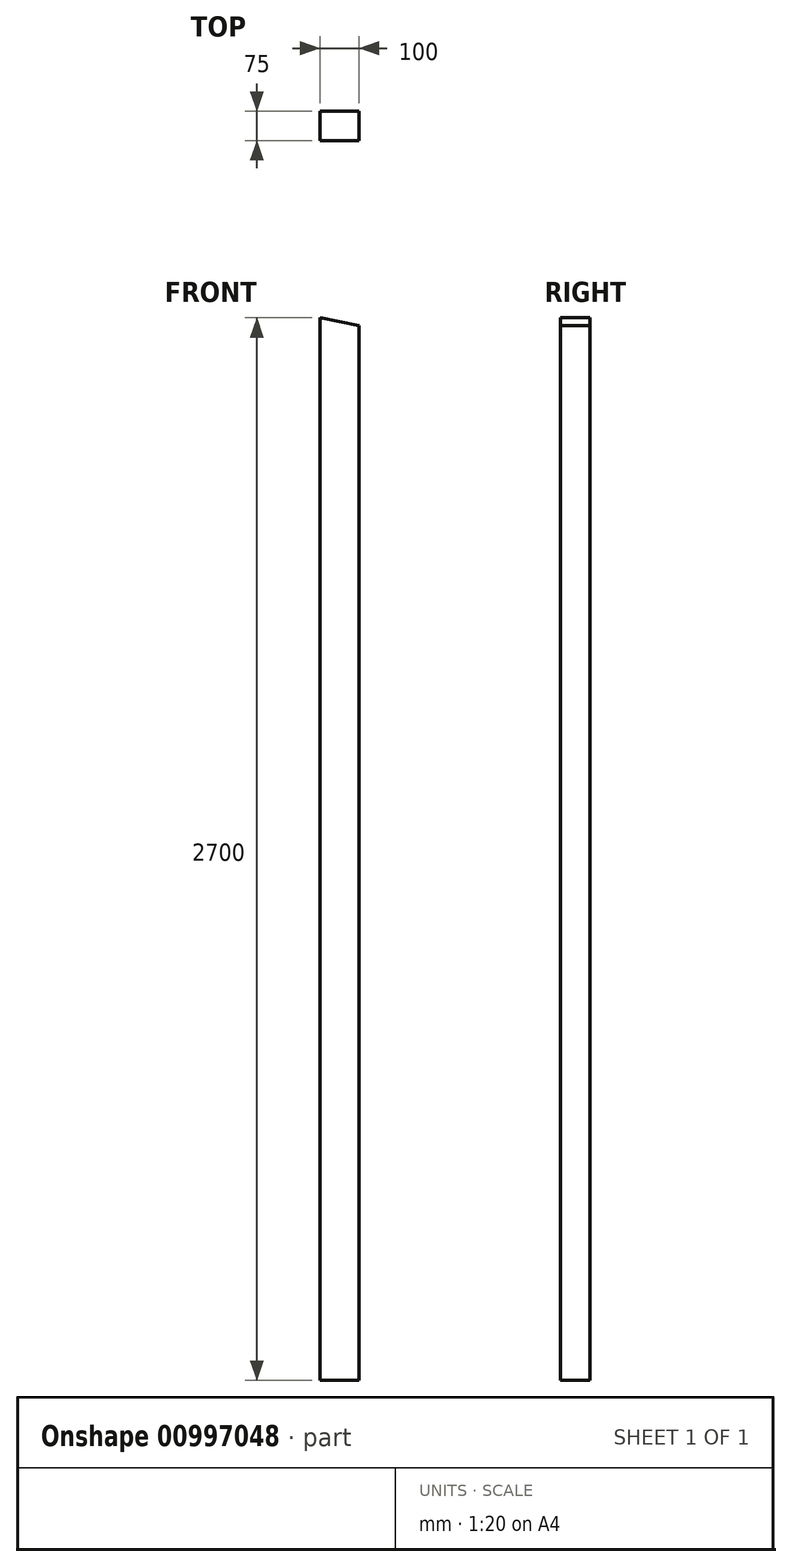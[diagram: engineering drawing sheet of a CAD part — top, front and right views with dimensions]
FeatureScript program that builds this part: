
annotation { "Feature Type Name" : "Feature", "Feature Type Description" : "" }
export const myFeature = defineFeature(function(context is Context, id is Id, definition is map)
    precondition{}
    {
        {
            var Q0;
            Q0=qCreatedBy(makeId("Top.planeOp"),FACE);
            var sketch = newSketch(context, id + "F0", { "sketchPlane" : qUnion([Q0])});
            skLineSegment(sketch, "E0.bottom", {"start": v(-89.27, 75) * mm, "end": v(10.73, 75) * mm});
            skLineSegment(sketch, "E0.top", {"start": v(-89.27, 0) * mm, "end": v(10.73, 0) * mm});
            skLineSegment(sketch, "E0.left", {"start": v(-89.27, 75) * mm, "end": v(-89.27, 0) * mm});
            skLineSegment(sketch, "E0.right", {"start": v(10.73, 75) * mm, "end": v(10.73, 0) * mm});
            skSolve(sketch);
        }
        {
            var Q0;
            Q0 = qSketchRegion(id + "F0", true);
            extrude(context, id + "F1", {"entities" : qUnion([Q0]), "depth" : 2700 * mm, "offsetDistance" : 25 * mm});
        }
        {
            var Q0;
            Q0=makeQuery(id+"F1.opExtrude","CAP_EDGE",EDGE,{"disambiguationData":[OSD([sQuery(id+"F0.wireOp",EDGE,"E0.right")])],"isStart":false});
            chamfer(context, id + "F2", {"entities" : qUnion([Q0]), "chamferType" : ChamferType.OFFSET_ANGLE, "width" : 100 * mm, "oppositeDirection" : true, "angle" : 11.3 * degree, "tangentPropagation" : true});
        }
    });
